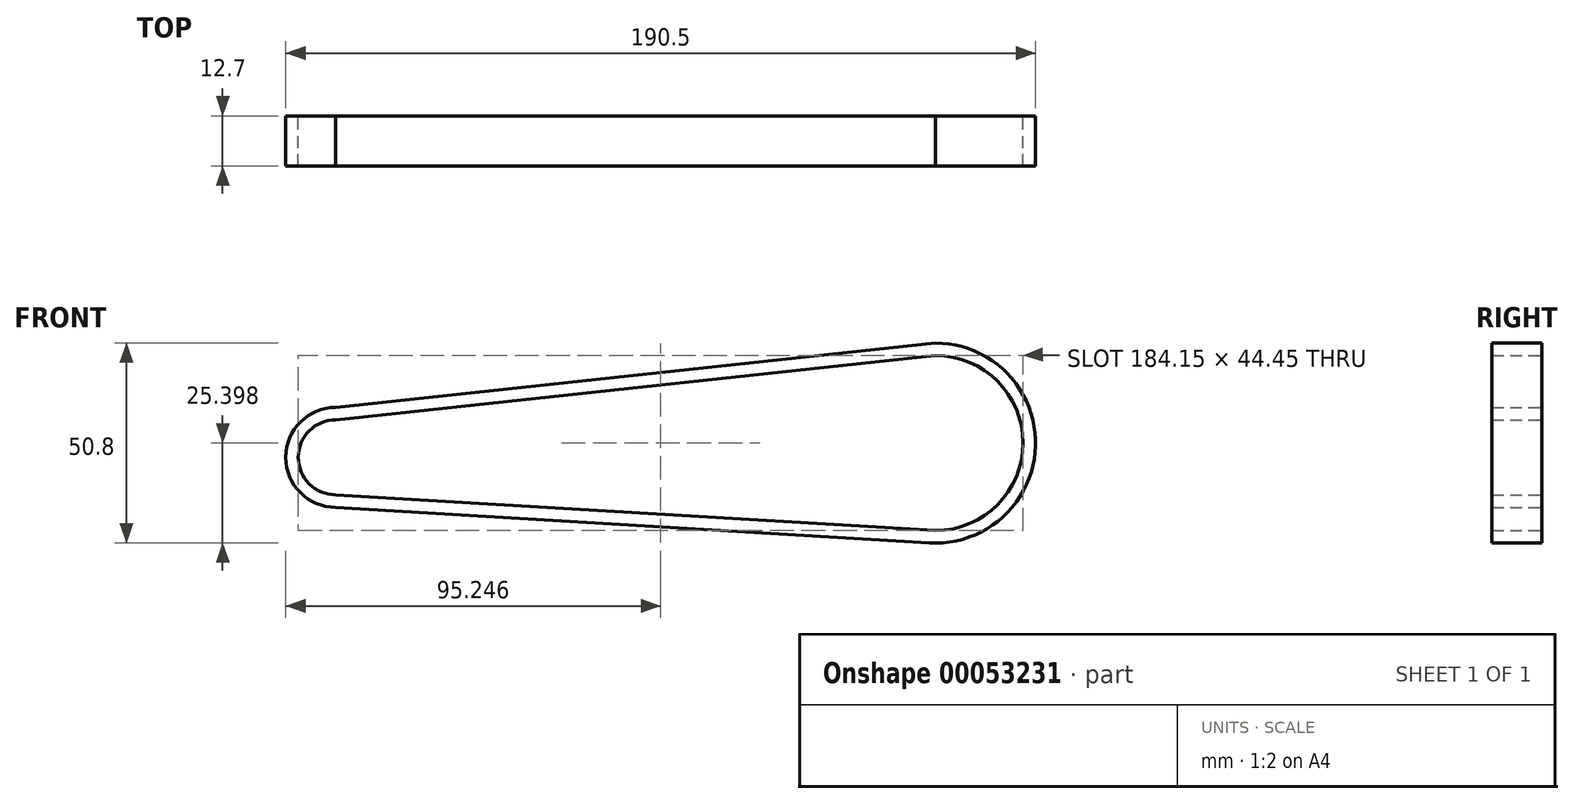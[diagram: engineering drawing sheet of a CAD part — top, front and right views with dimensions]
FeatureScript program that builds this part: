
annotation { "Feature Type Name" : "Feature", "Feature Type Description" : "" }
export const myFeature = defineFeature(function(context is Context, id is Id, definition is map)
    precondition{}
    {
        {
            var Q0;
            Q0=qCreatedBy(makeId("Front.planeOp"),FACE);
            var sketch = newSketch(context, id + "F0", { "sketchPlane" : qUnion([Q0])});
            skArc(sketch, "E0", {"start": v(-150.61, 16.97) * mm, "mid": v(-160.14, 7.45) * mm, "end": v(-150.61, -2.08) * mm});
            skArc(sketch, "E1", {"start": v(1.79, -11.15) * mm, "mid": v(24.01, 11.08) * mm, "end": v(1.79, 33.3) * mm});
            skLineSegment(sketch, "E2", {"start": v(-150.61, 16.97) * mm, "end": v(1.79, 33.3) * mm});
            skLineSegment(sketch, "E3", {"start": v(-150.61, -2.08) * mm, "end": v(1.79, -11.15) * mm});
            skArc(sketch, "E4", {"start": v(-150.61, 20.15) * mm, "mid": v(-163.31, 7.45) * mm, "end": v(-150.61, -5.25) * mm});
            skArc(sketch, "E5", {"start": v(0.27, -14.28) * mm, "mid": v(27.17, 10.32) * mm, "end": v(1.79, 36.48) * mm});
            skLineSegment(sketch, "E6", {"start": v(-150.61, 20.15) * mm, "end": v(1.79, 36.48) * mm});
            skLineSegment(sketch, "E7", {"start": v(-150.61, -5.25) * mm, "end": v(1.79, -14.37) * mm});
            skSolve(sketch);
        }
        {
            var Q0;
            Q0=makeQuery(id+"F0.imprint","IMPRINT",FACE,{"disambiguationData":[TD([[makeQuery(id+"F0.imprint","IMPRINT",EDGE,{"derivedFrom":sQuery(id+"F0.wireOp",EDGE,"E0")}),-1.0]])]});
            extrude(context, id + "F1", {"entities" : qUnion([Q0]), "depth" : 12.7 * mm});
        }
    });
